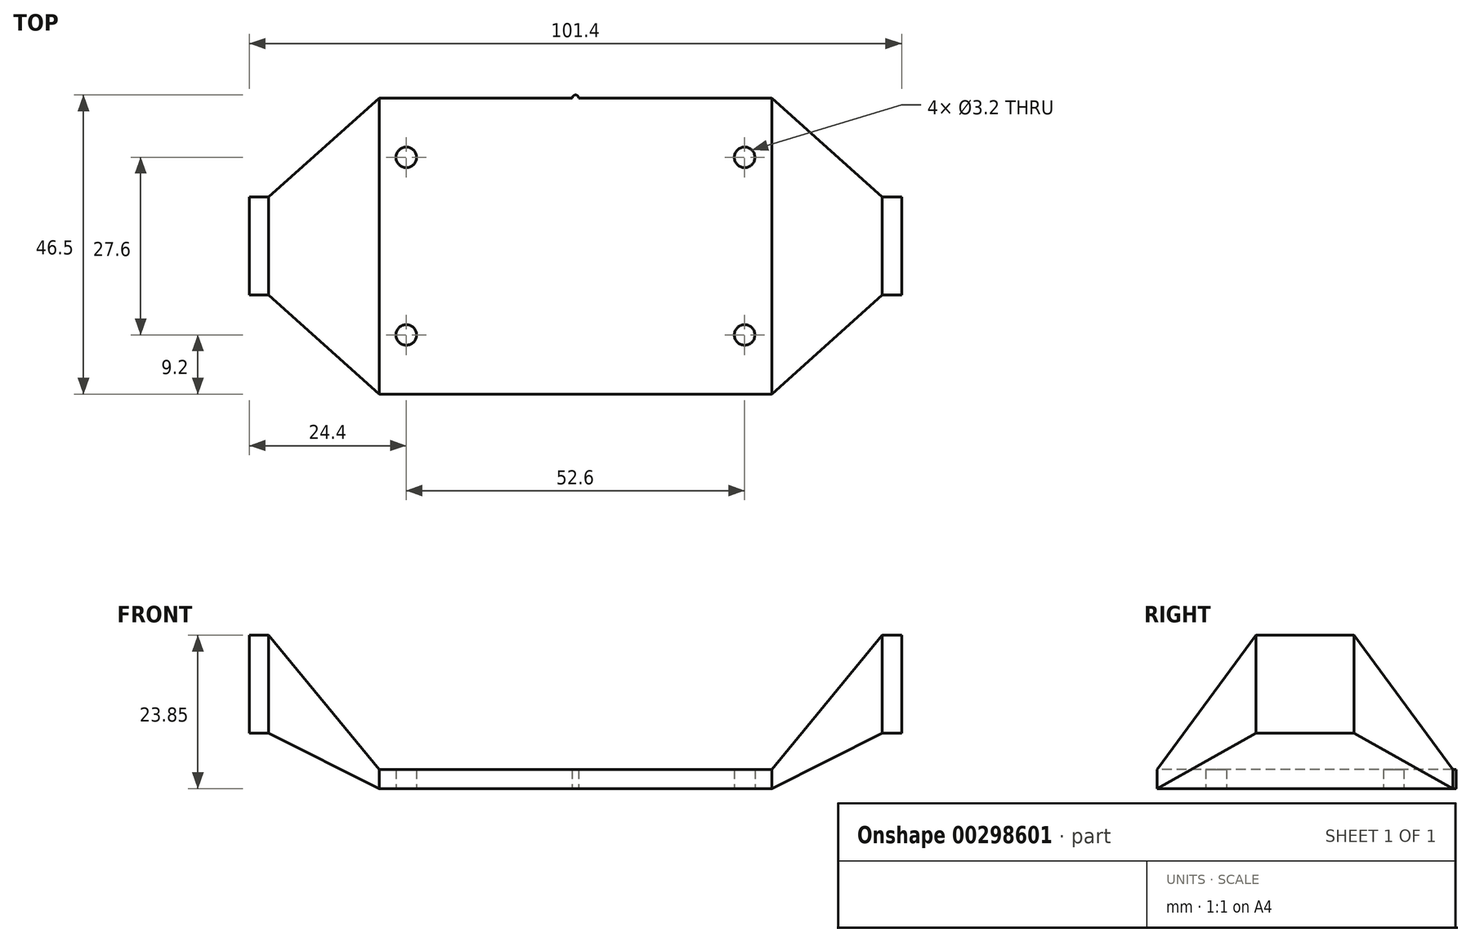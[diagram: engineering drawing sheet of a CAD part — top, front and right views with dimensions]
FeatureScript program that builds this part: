
annotation { "Feature Type Name" : "Feature", "Feature Type Description" : "" }
export const myFeature = defineFeature(function(context is Context, id is Id, definition is map)
    precondition{}
    {
        {
            var Q0;
            Q0=qCreatedBy(makeId("Top.planeOp"),FACE);
            var sketch = newSketch(context, id + "F0", { "sketchPlane" : qUnion([Q0])});
            skLineSegment(sketch, "E0.bottom", {"start": v(-30.5, 23) * mm, "end": v(30.5, 23) * mm});
            skLineSegment(sketch, "E0.top", {"start": v(-30.5, -23) * mm, "end": v(30.5, -23) * mm});
            skLineSegment(sketch, "E0.left", {"start": v(-30.5, 23) * mm, "end": v(-30.5, -23) * mm});
            skLineSegment(sketch, "E0.right", {"start": v(30.5, 23) * mm, "end": v(30.5, -23) * mm});
            skCircle(sketch, "E1", {"center": v(-26.3, 13.8) * mm, "radius": 1.6 * mm});
            skCircle(sketch, "E2", {"center": v(26.3, 13.8) * mm, "radius": 1.6 * mm});
            skCircle(sketch, "E3", {"center": v(26.3, -13.8) * mm, "radius": 1.6 * mm});
            skCircle(sketch, "E4", {"center": v(-26.3, -13.8) * mm, "radius": 1.6 * mm});
            skCircle(sketch, "E5", {"center": v(0, 23) * mm, "radius": 0.5 * mm});
            skPoint(sketch, "E6.endSnap0", {"position": v(30.5, 0) * mm});
            skSolve(sketch);
        }
        {
            var Q0;
            Q0 = qSketchRegion(id + "F0", true);
            extrude(context, id + "F1", {"entities" : qUnion([Q0]), "depth" : 3 * mm});
        }
        {
            var Q0;
            Q0=makeQuery(id+"F1.opExtrude","SWEPT_FACE",FACE,{"disambiguationData":[OSD([sQuery(id+"F0.wireOp",EDGE,"E0.right")])]});
            cPlane(context, id + "F2", {"entities" : qUnion([Q0]), "cplaneType" : CPlaneType.OFFSET, "offset" : 17.2 * mm, "width" : 150 * mm, "height" : 150 * mm});
        }
        {
            var Q0;
            Q0=qCreatedBy(id+"F2.planeOp",FACE);
            var sketch = newSketch(context, id + "F3", { "sketchPlane" : qUnion([Q0])});
            skLineSegment(sketch, "E7.bottom", {"start": v(-7.63, 23.85) * mm, "end": v(7.62, 23.85) * mm});
            skLineSegment(sketch, "E7.top", {"start": v(-7.63, 8.6) * mm, "end": v(7.62, 8.6) * mm});
            skLineSegment(sketch, "E7.left", {"start": v(-7.63, 23.85) * mm, "end": v(-7.63, 8.6) * mm});
            skLineSegment(sketch, "E7.right", {"start": v(7.62, 23.85) * mm, "end": v(7.62, 8.6) * mm});
            skSolve(sketch);
        }
        {
            var Q0;
            Q0 = qSketchRegion(id + "F3", true);
            extrude(context, id + "F4", {"entities" : qUnion([Q0]), "operationType" : NewBodyOperationType.ADD, "depth" : 3 * mm});
        }
        {
            var Q0;
            Q0=makeQuery(id+"F4.opExtrude","CAP_FACE",FACE,{"disambiguationData":[OSD([sQuery(id+"F3.wireOp",EDGE,"E7.bottom"),sQuery(id+"F3.wireOp",EDGE,"E7.top"),sQuery(id+"F3.wireOp",EDGE,"E7.left"),sQuery(id+"F3.wireOp",EDGE,"E7.right")])],"isStart":true});
            var Q1;
            Q1=makeQuery(id+"F1.opExtrude","SWEPT_FACE",FACE,{"disambiguationData":[OSD([sQuery(id+"F0.wireOp",EDGE,"E0.right")])]});
            loft(context, id + "F5", {"operationType" : NewBodyOperationType.ADD, "sheetProfilesArray" : [{ "sheetProfileEntities" : qUnion([Q0]) }, { "sheetProfileEntities" : qUnion([Q1]) }]});
        }
        {
            var Q0;
            Q0=makeQuery(id+"F1.opExtrude","SWEPT_FACE",FACE,{"disambiguationData":[OSD([sQuery(id+"F0.wireOp",EDGE,"E0.left")])]});
            cPlane(context, id + "F6", {"entities" : qUnion([Q0]), "cplaneType" : CPlaneType.OFFSET, "offset" : 17.2 * mm, "width" : 150 * mm, "height" : 150 * mm});
        }
        {
            var Q0;
            Q0=qCreatedBy(id+"F6.planeOp",FACE);
            var sketch = newSketch(context, id + "F7", { "sketchPlane" : qUnion([Q0])});
            skLineSegment(sketch, "E8.bottom", {"start": v(-7.63, 23.85) * mm, "end": v(7.62, 23.85) * mm});
            skLineSegment(sketch, "E8.top", {"start": v(-7.63, 8.6) * mm, "end": v(7.62, 8.6) * mm});
            skLineSegment(sketch, "E8.left", {"start": v(-7.63, 23.85) * mm, "end": v(-7.63, 8.6) * mm});
            skLineSegment(sketch, "E8.right", {"start": v(7.62, 23.85) * mm, "end": v(7.62, 8.6) * mm});
            skSolve(sketch);
        }
        {
            var Q0;
            Q0 = qSketchRegion(id + "F7", true);
            extrude(context, id + "F8", {"entities" : qUnion([Q0]), "depth" : 3 * mm});
        }
        {
            var Q0;
            Q0=makeQuery(id+"F8.opExtrude","CAP_FACE",FACE,{"disambiguationData":[OSD([sQuery(id+"F7.wireOp",EDGE,"E8.bottom"),sQuery(id+"F7.wireOp",EDGE,"E8.top"),sQuery(id+"F7.wireOp",EDGE,"E8.left"),sQuery(id+"F7.wireOp",EDGE,"E8.right")])],"isStart":true});
            var Q1;
            Q1=makeQuery(id+"F1.opExtrude","SWEPT_FACE",FACE,{"disambiguationData":[OSD([sQuery(id+"F0.wireOp",EDGE,"E0.left")])]});
            loft(context, id + "F9", {"operationType" : NewBodyOperationType.ADD, "sheetProfilesArray" : [{ "sheetProfileEntities" : qUnion([Q0]) }, { "sheetProfileEntities" : qUnion([Q1]) }]});
        }
    });
